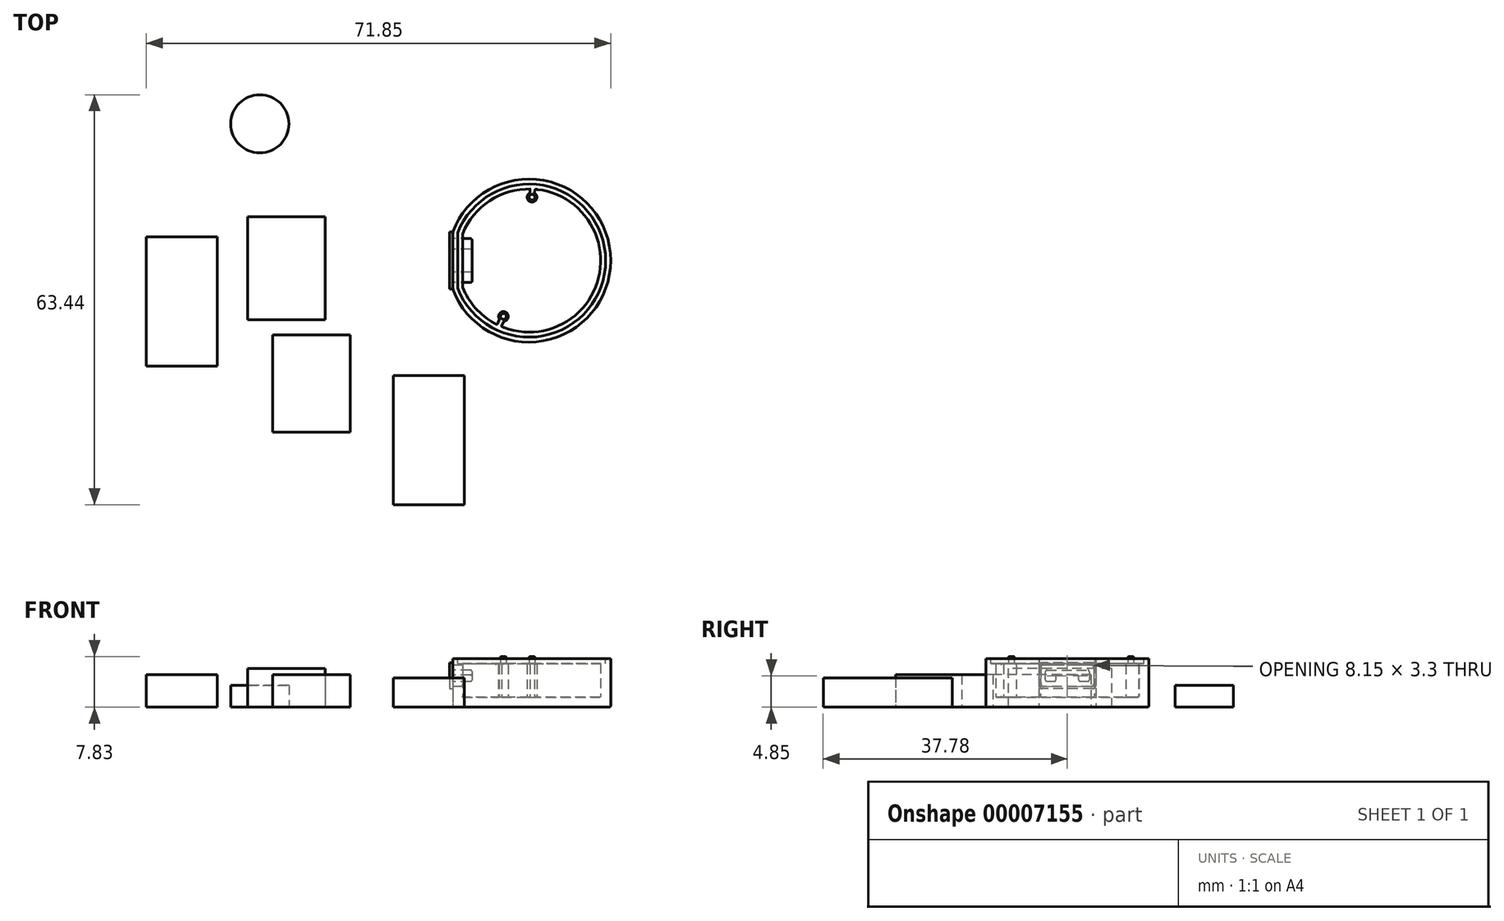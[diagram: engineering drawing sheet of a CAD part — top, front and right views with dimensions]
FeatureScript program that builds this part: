
annotation { "Feature Type Name" : "Feature", "Feature Type Description" : "" }
export const myFeature = defineFeature(function(context is Context, id is Id, definition is map)
    precondition{}
    {
        {
            var Q0;
            Q0=qCreatedBy(makeId("Top.planeOp"),FACE);
            var sketch = newSketch(context, id + "F0", { "sketchPlane" : qUnion([Q0])});
            skCircle(sketch, "E0", {"center": v(0, 0) * mm, "radius": 12.62 * mm});
            skLineSegment(sketch, "E1.bottom", {"start": v(-11.82, 4.42) * mm, "end": v(-39.46, 4.42) * mm});
            skLineSegment(sketch, "E1.top", {"start": v(-11.82, -4.42) * mm, "end": v(-39.46, -4.43) * mm});
            skLineSegment(sketch, "E1.left", {"start": v(-11.82, 4.43) * mm, "end": v(-11.82, -4.42) * mm});
            skLineSegment(sketch, "E1.right", {"start": v(-39.46, 4.42) * mm, "end": v(-39.46, -4.43) * mm});
            skSolve(sketch);
        }
        {
            var Q0;
            {var subQ0=sQuery(id+"F0.wireOp",EDGE,"E1.left");Q0=makeQuery(id+"F0.imprint","IMPRINT",FACE,{"disambiguationData":[TD([[makeQuery(id+"F0.imprint","IMPRINT",EDGE,{"derivedFrom":subQ0}),1.0]])]});}
            extrude(context, id + "F1", {"entities" : qUnion([Q0]), "depth" : 7.5 * mm});
        }
        {
            var Q0;
            Q0=makeQuery(id+"F1.opExtrude","CAP_FACE",FACE,{"disambiguationData":[OSD([sQuery(id+"F0.wireOp",EDGE,"E0"),sQuery(id+"F0.wireOp",EDGE,"E1.left")])],"isStart":false});
            shell(context, id + "F2", {"entities" : qUnion([Q0]), "thickness" : 1.55 * mm});
        }
        {
            var Q0;
            Q0=makeQuery(id+"F1.opExtrude","CAP_FACE",FACE,{"disambiguationData":[OSD([sQuery(id+"F0.wireOp",EDGE,"E0"),sQuery(id+"F0.wireOp",EDGE,"E1.left")])],"isStart":false});
            var sketch = newSketch(context, id + "F3", { "sketchPlane" : qUnion([Q0])});
            skLineSegment(sketch, "E2", {"start": v(-11.82, 4.42) * mm, "end": v(-10.27, 4.13) * mm, "construction": true});
            skLineSegment(sketch, "E3", {"start": v(-11.82, -4.42) * mm, "end": v(-10.27, -4.13) * mm, "construction": true});
            skCircle(sketch, "E4", {"center": v(0, 0) * mm, "radius": 11.85 * mm});
            skLineSegment(sketch, "E5", {"start": v(-11.05, 4.28) * mm, "end": v(-11.05, -4.28) * mm});
            skSolve(sketch);
        }
        {
            var Q0;
            {var subQ2=sQuery(id+"F3.wireOp",EDGE,"E5");Q0=makeQuery(id+"F3.imprint","IMPRINT",FACE,{"disambiguationData":[TD([[makeQuery(id+"F3.imprint","IMPRINT",EDGE,{"derivedFrom":subQ2}),1.0]])]});}
            extrude(context, id + "F4", {"entities" : qUnion([Q0]), "operationType" : NewBodyOperationType.REMOVE, "oppositeDirection" : true, "depth" : .775 * mm});
        }
        {
            var Q0;
            Q0=makeQuery(id+"F2.opShell","OFFSET_FACE",FACE,{"disambiguationData":[OSD([sQuery(id+"F0.wireOp",EDGE,"E0"),sQuery(id+"F0.wireOp",EDGE,"E1.left")])]});
            var sketch = newSketch(context, id + "F5", { "sketchPlane" : qUnion([Q0])});
            skLineSegment(sketch, "E6", {"start": v(0, 0) * mm, "end": v(0, 11.08) * mm, "construction": true});
            skCircle(sketch, "E7", {"center": v(0.46, 9.8) * mm, "radius": 0.75 * mm});
            skLineSegment(sketch, "E8", {"start": v(0, 0) * mm, "end": v(0, -11.08) * mm});
            skCircle(sketch, "E9", {"center": v(-3.97, -8.64) * mm, "radius": 0.75 * mm});
            skLineSegment(sketch, "E10", {"start": v(0, 0) * mm, "end": v(0.67, 14.46) * mm, "construction": true});
            skLineSegment(sketch, "E11", {"start": v(0.9, 11.1) * mm, "end": v(0.84, 9.9) * mm});
            skLineSegment(sketch, "E12", {"start": v(0.84, 9.9) * mm, "end": v(0.09, 9.93) * mm});
            skLineSegment(sketch, "E13", {"start": v(0.09, 9.93) * mm, "end": v(0.14, 11.14) * mm});
            skLineSegment(sketch, "E14", {"start": v(0.14, 11.14) * mm, "end": v(0.9, 11.1) * mm});
            skLineSegment(sketch, "E15", {"start": v(0, 0) * mm, "end": v(-6.04, -13.15) * mm, "construction": true});
            skLineSegment(sketch, "E16", {"start": v(-5.02, -10.04) * mm, "end": v(-4.3, -8.48) * mm});
            skLineSegment(sketch, "E17", {"start": v(-4.3, -8.48) * mm, "end": v(-3.62, -8.79) * mm});
            skLineSegment(sketch, "E18", {"start": v(-3.62, -8.79) * mm, "end": v(-4.35, -10.38) * mm});
            skLineSegment(sketch, "E19", {"start": v(-4.35, -10.38) * mm, "end": v(-5.02, -10.04) * mm});
            skSolve(sketch);
        }
        {
            var Q0;
            {var subQ4=sQuery(id+"F5.wireOp",EDGE,"E11");var subQ6=sQuery(id+"F5.wireOp",EDGE,"E7");var subQ8=makeQuery(id+"F5.imprint","INTERSECT",VERTEX,{"derivedFrom":[subQ6,subQ4]});Q0=makeQuery(id+"F5.imprint","IMPRINT",FACE,{"disambiguationData":[TD([[makeQuery(id+"F5.imprint","IMPRINT",EDGE,{"disambiguationData":[TD([[subQ8,-1.0]])],"derivedFrom":subQ6}),-1.0]])]});}
            var Q1;
            {var subQ3=sQuery(id+"F5.wireOp",EDGE,"E12");Q1=makeQuery(id+"F5.imprint","IMPRINT",FACE,{"disambiguationData":[TD([[makeQuery(id+"F5.imprint","IMPRINT",EDGE,{"derivedFrom":subQ3}),-1.0]])]});}
            var Q2;
            {var subQ3=sQuery(id+"F5.wireOp",EDGE,"E12");Q2=makeQuery(id+"F5.imprint","IMPRINT",FACE,{"disambiguationData":[TD([[makeQuery(id+"F5.imprint","IMPRINT",EDGE,{"derivedFrom":subQ3}),1.0]])]});}
            var Q3;
            {var subQ3=sQuery(id+"F5.wireOp",EDGE,"E17");Q3=makeQuery(id+"F5.imprint","IMPRINT",FACE,{"disambiguationData":[TD([[makeQuery(id+"F5.imprint","IMPRINT",EDGE,{"derivedFrom":subQ3}),1.0]])]});}
            var Q4;
            {var subQ3=sQuery(id+"F5.wireOp",EDGE,"E17");Q4=makeQuery(id+"F5.imprint","IMPRINT",FACE,{"disambiguationData":[TD([[makeQuery(id+"F5.imprint","IMPRINT",EDGE,{"derivedFrom":subQ3}),-1.0]])]});}
            var Q5;
            {var subQ4=sQuery(id+"F5.wireOp",EDGE,"E16");var subQ6=sQuery(id+"F5.wireOp",EDGE,"E9");var subQ8=makeQuery(id+"F5.imprint","INTERSECT",VERTEX,{"derivedFrom":[subQ6,subQ4]});Q5=makeQuery(id+"F5.imprint","IMPRINT",FACE,{"disambiguationData":[TD([[makeQuery(id+"F5.imprint","IMPRINT",EDGE,{"disambiguationData":[TD([[subQ8,-1.0]])],"derivedFrom":subQ6}),-1.0]])]});}
            var Q6;
            Q6=makeQuery(id+"F4.boolean.opBoolean","COPY",FACE,{"derivedFrom":makeQuery(id+"F4.opExtrude","CAP_FACE",FACE,{"disambiguationData":[OSD([sQuery(id+"F0.wireOp",EDGE,"E0"),sQuery(id+"F0.wireOp",EDGE,"E1.left"),sQuery(id+"F3.wireOp",EDGE,"E4"),sQuery(id+"F3.wireOp",EDGE,"E5")])],"isStart":false})});
            extrude(context, id + "F6", {"entities" : qUnion([Q0, Q1, Q2, Q3, Q4, Q5]), "operationType" : NewBodyOperationType.ADD, "endBound" : BoundingType.UP_TO_SURFACE, "endBoundEntityFace" : qUnion([Q6]), "depth" : 5 * mm});
        }
        {
            var Q0;
            {var subQ0=sQuery(id+"F0.wireOp",EDGE,"E0");Q0=makeQuery(id+"F6.boolean.opBoolean","MERGE",FACE,{"derivedFrom":[makeQuery(id+"F4.boolean.opBoolean","COPY",FACE,{"derivedFrom":makeQuery(id+"F4.opExtrude","CAP_FACE",FACE,{"disambiguationData":[OSD([subQ0,sQuery(id+"F0.wireOp",EDGE,"E1.left"),sQuery(id+"F3.wireOp",EDGE,"E4"),sQuery(id+"F3.wireOp",EDGE,"E5")])],"isStart":false})}),makeQuery(id+"F6.opExtrude","CAP_FACE",FACE,{"disambiguationData":[OSD([subQ0,sQuery(id+"F5.wireOp",EDGE,"E7"),sQuery(id+"F5.wireOp",EDGE,"E11"),sQuery(id+"F5.wireOp",EDGE,"E13")])],"isStart":false}),makeQuery(id+"F6.opExtrude","CAP_FACE",FACE,{"disambiguationData":[OSD([subQ0,sQuery(id+"F5.wireOp",EDGE,"E9"),sQuery(id+"F5.wireOp",EDGE,"E16"),sQuery(id+"F5.wireOp",EDGE,"E18")])],"isStart":false})]});}
            var sketch = newSketch(context, id + "F7", { "sketchPlane" : qUnion([Q0])});
            skCircle(sketch, "E20", {"center": v(0.46, 9.8) * mm, "radius": 0.45 * mm});
            skCircle(sketch, "E21", {"center": v(-3.97, -8.64) * mm, "radius": 0.45 * mm});
            skSolve(sketch);
        }
        {
            var Q0;
            Q0=makeQuery(id+"F7.imprint","IMPRINT",FACE,{"disambiguationData":[TD([[makeQuery(id+"F7.imprint","IMPRINT",EDGE,{"derivedFrom":sQuery(id+"F7.wireOp",EDGE,"E20")}),1.0]])]});
            var Q1;
            Q1=makeQuery(id+"F7.imprint","IMPRINT",FACE,{"disambiguationData":[TD([[makeQuery(id+"F7.imprint","IMPRINT",EDGE,{"derivedFrom":sQuery(id+"F7.wireOp",EDGE,"E21")}),1.0]])]});
            extrude(context, id + "F8", {"entities" : qUnion([Q0, Q1]), "operationType" : NewBodyOperationType.ADD, "depth" : 1.1 * mm});
        }
        {
            var Q0;
            Q0=makeQuery(id+"F1.opExtrude","SWEPT_FACE",FACE,{"disambiguationData":[OSD([sQuery(id+"F0.wireOp",EDGE,"E1.left")])]});
            var sketch = newSketch(context, id + "F9", { "sketchPlane" : qUnion([Q0])});
            skLineSegment(sketch, "E22.bottom", {"start": v(-3.73, 6.5) * mm, "end": v(3.73, 6.5) * mm});
            skLineSegment(sketch, "E22.top", {"start": v(-3.73, 3.2) * mm, "end": v(3.73, 3.2) * mm});
            skLineSegment(sketch, "E22.left", {"start": v(-4.08, 6.15) * mm, "end": v(-4.08, 3.55) * mm});
            skLineSegment(sketch, "E22.right", {"start": v(4.08, 6.15) * mm, "end": v(4.08, 3.55) * mm});
            skLineSegment(sketch, "E23", {"start": v(0, 0) * mm, "end": v(0, 7.5) * mm, "construction": true});
            skPoint(sketch, "E24.visualSharp", {"position": v(-4.08, 6.5) * mm});
            skArc(sketch, "E24.filletArc", {"start": v(-3.73, 6.5) * mm, "mid": v(-3.97, 6.4) * mm, "end": v(-4.08, 6.15) * mm});
            skPoint(sketch, "E25.visualSharp", {"position": v(-4.08, 3.2) * mm});
            skArc(sketch, "E25.filletArc", {"start": v(-4.08, 3.55) * mm, "mid": v(-3.97, 3.3) * mm, "end": v(-3.73, 3.2) * mm});
            skPoint(sketch, "E26.visualSharp", {"position": v(4.08, 3.2) * mm});
            skArc(sketch, "E26.filletArc", {"start": v(3.73, 3.2) * mm, "mid": v(3.97, 3.3) * mm, "end": v(4.08, 3.55) * mm});
            skPoint(sketch, "E27.visualSharp", {"position": v(4.08, 6.5) * mm});
            skArc(sketch, "E27.filletArc", {"start": v(4.08, 6.15) * mm, "mid": v(3.97, 6.4) * mm, "end": v(3.73, 6.5) * mm});
            skSolve(sketch);
        }
        {
            var Q0;
            Q0=makeQuery(id+"F9.imprint","IMPRINT",FACE,{"disambiguationData":[TD([[makeQuery(id+"F9.imprint","IMPRINT",EDGE,{"derivedFrom":sQuery(id+"F9.wireOp",EDGE,"E22.bottom")}),-1.0]])]});
            extrude(context, id + "F10", {"entities" : qUnion([Q0]), "operationType" : NewBodyOperationType.REMOVE, "endBound" : BoundingType.UP_TO_NEXT, "oppositeDirection" : true, "depth" : 25 * mm});
        }
        {
            var Q0;
            Q0=makeQuery(id+"F1.opExtrude","CAP_EDGE",EDGE,{"disambiguationData":[OSD([sQuery(id+"F0.wireOp",EDGE,"E0")])],"isStart":true});
            var Q1;
            Q1=makeQuery(id+"F1.opExtrude","CAP_EDGE",EDGE,{"disambiguationData":[OSD([sQuery(id+"F0.wireOp",EDGE,"E1.left")])],"isStart":true});
            fillet(context, id + "F11", {"entities" : qUnion([Q0, Q1]), "radius" : .25 * mm, "tangentPropagation" : true, "allowEdgeOverflow" : false});
        }
        {
            var Q0;
            Q0=makeQuery(id+"F10.boolean.opBoolean","COPY",EDGE,{"derivedFrom":makeQuery(id+"F10.opExtrude","CAP_EDGE",EDGE,{"disambiguationData":[OSD([sQuery(id+"F9.wireOp",EDGE,"E22.top")])],"isStart":true})});
            var Q1;
            Q1=makeQuery(id+"F10.boolean.opBoolean","COPY",EDGE,{"derivedFrom":makeQuery(id+"F10.opExtrude","CAP_EDGE",EDGE,{"disambiguationData":[OSD([sQuery(id+"F9.wireOp",EDGE,"E22.top")])],"isStart":false})});
            var Q2;
            Q2=makeQuery(id+"F6.opExtrude","CAP_EDGE",EDGE,{"disambiguationData":[OSD([sQuery(id+"F5.wireOp",EDGE,"E9")])],"isStart":false});
            var Q3;
            Q3=makeQuery(id+"F6.opExtrude","CAP_EDGE",EDGE,{"disambiguationData":[OSD([sQuery(id+"F5.wireOp",EDGE,"E18")])],"isStart":false});
            var Q4;
            Q4=makeQuery(id+"F8.opExtrude","CAP_EDGE",EDGE,{"disambiguationData":[OSD([sQuery(id+"F7.wireOp",EDGE,"E21")])],"isStart":false});
            var Q5;
            Q5=makeQuery(id+"F6.opExtrude","CAP_EDGE",EDGE,{"disambiguationData":[OSD([sQuery(id+"F5.wireOp",EDGE,"E16")])],"isStart":false});
            var Q6;
            Q6=makeQuery(id+"F6.opExtrude","SWEPT_EDGE",EDGE,{"disambiguationData":[OSD([sQuery(id+"F0.wireOp",EDGE,"E0"),sQuery(id+"F5.wireOp",EDGE,"E16")])]});
            var Q7;
            Q7=makeQuery(id+"F6.opExtrude","CAP_EDGE",EDGE,{"disambiguationData":[OSD([sQuery(id+"F5.wireOp",EDGE,"E9")])],"isStart":true});
            var Q8;
            Q8=makeQuery(id+"F6.opExtrude","CAP_EDGE",EDGE,{"disambiguationData":[OSD([sQuery(id+"F5.wireOp",EDGE,"E16")])],"isStart":true});
            var Q9;
            Q9=makeQuery(id+"F6.opExtrude","CAP_EDGE",EDGE,{"disambiguationData":[OSD([sQuery(id+"F5.wireOp",EDGE,"E18")])],"isStart":true});
            var Q10;
            Q10=makeQuery(id+"F6.opExtrude","SWEPT_EDGE",EDGE,{"disambiguationData":[OSD([sQuery(id+"F5.wireOp",EDGE,"E9"),sQuery(id+"F5.wireOp",EDGE,"E18")])]});
            var Q11;
            Q11=makeQuery(id+"F6.opExtrude","SWEPT_EDGE",EDGE,{"disambiguationData":[OSD([sQuery(id+"F0.wireOp",EDGE,"E0"),sQuery(id+"F5.wireOp",EDGE,"E18")])]});
            var Q12;
            Q12=makeQuery(id+"F6.opExtrude","SWEPT_EDGE",EDGE,{"disambiguationData":[OSD([sQuery(id+"F5.wireOp",EDGE,"E9"),sQuery(id+"F5.wireOp",EDGE,"E16")])]});
            var Q13;
            Q13=makeQuery(id+"F6.opExtrude","CAP_EDGE",EDGE,{"disambiguationData":[OSD([sQuery(id+"F5.wireOp",EDGE,"E13")])],"isStart":false});
            var Q14;
            Q14=makeQuery(id+"F6.opExtrude","CAP_EDGE",EDGE,{"disambiguationData":[OSD([sQuery(id+"F5.wireOp",EDGE,"E7")])],"isStart":false});
            var Q15;
            Q15=makeQuery(id+"F8.opExtrude","CAP_EDGE",EDGE,{"disambiguationData":[OSD([sQuery(id+"F7.wireOp",EDGE,"E20")])],"isStart":false});
            var Q16;
            Q16=makeQuery(id+"F6.opExtrude","CAP_EDGE",EDGE,{"disambiguationData":[OSD([sQuery(id+"F5.wireOp",EDGE,"E11")])],"isStart":false});
            var Q17;
            {var subQ0=sQuery(id+"F5.wireOp",EDGE,"E13");var subQ1=sQuery(id+"F0.wireOp",EDGE,"E0");Q17=makeQuery(id+"F6.boolean.opBoolean","SPLIT",EDGE,{"disambiguationData":[TD([makeQuery(id+"F6.opExtrude","SWEPT_FACE",FACE,{"disambiguationData":[OSD([subQ0])]})])],"derivedFrom":makeQuery(id+"F4.boolean.opBoolean","COPY",EDGE,{"derivedFrom":makeQuery(id+"F4.opExtrude","CAP_EDGE",EDGE,{"disambiguationData":[OSD([subQ1])],"isStart":false})})});}
            var Q18;
            Q18=makeQuery(id+"F6.opExtrude","SWEPT_EDGE",EDGE,{"disambiguationData":[OSD([sQuery(id+"F5.wireOp",EDGE,"E7"),sQuery(id+"F5.wireOp",EDGE,"E13")])]});
            var Q19;
            Q19=makeQuery(id+"F6.opExtrude","CAP_EDGE",EDGE,{"disambiguationData":[OSD([sQuery(id+"F5.wireOp",EDGE,"E13")])],"isStart":true});
            var Q20;
            Q20=makeQuery(id+"F6.opExtrude","CAP_EDGE",EDGE,{"disambiguationData":[OSD([sQuery(id+"F5.wireOp",EDGE,"E7")])],"isStart":true});
            var Q21;
            Q21=makeQuery(id+"F6.opExtrude","SWEPT_EDGE",EDGE,{"disambiguationData":[OSD([sQuery(id+"F5.wireOp",EDGE,"E7"),sQuery(id+"F5.wireOp",EDGE,"E11")])]});
            var Q22;
            Q22=makeQuery(id+"F6.opExtrude","SWEPT_EDGE",EDGE,{"disambiguationData":[OSD([sQuery(id+"F0.wireOp",EDGE,"E0"),sQuery(id+"F5.wireOp",EDGE,"E11")])]});
            var Q23;
            Q23=makeQuery(id+"F6.opExtrude","CAP_EDGE",EDGE,{"disambiguationData":[OSD([sQuery(id+"F5.wireOp",EDGE,"E11")])],"isStart":true});
            var Q24;
            {var subQ0=sQuery(id+"F0.wireOp",EDGE,"E0");Q24=makeQuery(id+"F6.boolean.opBoolean","SPLIT",EDGE,{"disambiguationData":[TD([makeQuery(id+"F6.opExtrude","SWEPT_FACE",FACE,{"disambiguationData":[OSD([sQuery(id+"F5.wireOp",EDGE,"E11")])]})])],"derivedFrom":makeQuery(id+"F2.opShell","OFFSET_EDGE",EDGE,{"disambiguationData":[OSD([subQ0]),TDD([makeQuery(id+"F1.opExtrude","CAP_EDGE",EDGE,{"disambiguationData":[OSD([subQ0])],"isStart":true})])]})});}
            var Q25;
            {var subQ0=sQuery(id+"F0.wireOp",EDGE,"E0");Q25=makeQuery(id+"F6.boolean.opBoolean","SPLIT",EDGE,{"disambiguationData":[TD([makeQuery(id+"F6.opExtrude","SWEPT_FACE",FACE,{"disambiguationData":[OSD([sQuery(id+"F5.wireOp",EDGE,"E13")])]})])],"derivedFrom":makeQuery(id+"F2.opShell","OFFSET_EDGE",EDGE,{"disambiguationData":[OSD([subQ0]),TDD([makeQuery(id+"F1.opExtrude","CAP_EDGE",EDGE,{"disambiguationData":[OSD([subQ0])],"isStart":true})])]})});}
            fillet(context, id + "F12", {"entities" : qUnion([Q0, Q1, Q2, Q3, Q4, Q5, Q6, Q7, Q8, Q9, Q10, Q11, Q12, Q13, Q14, Q15, Q16, Q17, Q18, Q19, Q20, Q21, Q22, Q23, Q24, Q25]), "radius" : .15 * mm, "tangentPropagation" : true, "allowEdgeOverflow" : false});
        }
        {
            var Q0;
            Q0=makeQuery(id+"F1.opExtrude","SWEPT_FACE",FACE,{"disambiguationData":[OSD([sQuery(id+"F0.wireOp",EDGE,"E1.left")])]});
            var sketch = newSketch(context, id + "F13", { "sketchPlane" : qUnion([Q0])});
            skLineSegment(sketch, "E28.rect.bottom", {"start": v(-3.93, 2.85) * mm, "end": v(3.93, 2.85) * mm});
            skLineSegment(sketch, "E28.rect.top", {"start": v(-3.93, 6.85) * mm, "end": v(3.93, 6.85) * mm});
            skLineSegment(sketch, "E28.rect.left", {"start": v(-4.43, 3.35) * mm, "end": v(-4.43, 6.35) * mm});
            skLineSegment(sketch, "E28.rect.right", {"start": v(4.43, 3.35) * mm, "end": v(4.43, 6.35) * mm});
            skPoint(sketch, "E28.rect.middle", {"position": v(0, 4.85) * mm});
            skPoint(sketch, "E29.visualSharp", {"position": v(-4.43, 6.85) * mm});
            skArc(sketch, "E29.filletArc", {"start": v(-3.93, 6.85) * mm, "mid": v(-4.28, 6.7) * mm, "end": v(-4.43, 6.35) * mm});
            skPoint(sketch, "E30.visualSharp", {"position": v(-4.43, 2.85) * mm});
            skArc(sketch, "E30.filletArc", {"start": v(-4.43, 3.35) * mm, "mid": v(-4.28, 3) * mm, "end": v(-3.93, 2.85) * mm});
            skPoint(sketch, "E31.visualSharp", {"position": v(4.43, 2.85) * mm});
            skArc(sketch, "E31.filletArc", {"start": v(3.93, 2.85) * mm, "mid": v(4.28, 3) * mm, "end": v(4.43, 3.35) * mm});
            skPoint(sketch, "E32.visualSharp", {"position": v(4.43, 6.85) * mm});
            skArc(sketch, "E32.filletArc", {"start": v(4.43, 6.35) * mm, "mid": v(4.28, 6.7) * mm, "end": v(3.93, 6.85) * mm});
            skSolve(sketch);
        }
        {
            var Q0;
            Q0 = qSketchRegion(id + "F13", true);
            extrude(context, id + "F14", {"entities" : qUnion([Q0]), "depth" : .5 * mm});
        }
        {
            var Q0;
            Q0=makeQuery(id+"F14.opExtrude","CAP_FACE",FACE,{"disambiguationData":[OSD([sQuery(id+"F13.wireOp",EDGE,"E28.rect.bottom"),sQuery(id+"F13.wireOp",EDGE,"E28.rect.top"),sQuery(id+"F13.wireOp",EDGE,"E28.rect.left"),sQuery(id+"F13.wireOp",EDGE,"E28.rect.right"),sQuery(id+"F13.wireOp",EDGE,"E29.filletArc"),sQuery(id+"F13.wireOp",EDGE,"E30.filletArc"),sQuery(id+"F13.wireOp",EDGE,"E31.filletArc"),sQuery(id+"F13.wireOp",EDGE,"E32.filletArc")])],"isStart":true});
            var sketch = newSketch(context, id + "F15", { "sketchPlane" : qUnion([Q0])});
            skLineSegment(sketch, "E33", {"start": v(0, 6.85) * mm, "end": v(0, 2.85) * mm, "construction": true});
            skLineSegment(sketch, "E34", {"start": v(-4.43, 4.85) * mm, "end": v(4.43, 4.85) * mm, "construction": true});
            skLineSegment(sketch, "E35", {"start": v(-3.15, 5.72) * mm, "end": v(3.15, 5.72) * mm});
            skLineSegment(sketch, "E36", {"start": v(3.4, 5.47) * mm, "end": v(3.4, 4.22) * mm});
            skLineSegment(sketch, "E37", {"start": v(3.15, 3.97) * mm, "end": v(2.02, 3.97) * mm});
            skLineSegment(sketch, "E38", {"start": v(1.77, 4.22) * mm, "end": v(1.77, 4.7) * mm});
            skLineSegment(sketch, "E39", {"start": v(1.53, 4.95) * mm, "end": v(-1.53, 4.95) * mm});
            skLineSegment(sketch, "E40", {"start": v(-1.77, 4.7) * mm, "end": v(-1.77, 4.22) * mm});
            skLineSegment(sketch, "E41", {"start": v(-2.02, 3.97) * mm, "end": v(-3.15, 3.97) * mm});
            skLineSegment(sketch, "E42", {"start": v(-3.4, 4.22) * mm, "end": v(-3.4, 5.47) * mm});
            skPoint(sketch, "E43.visualSharp", {"position": v(-3.4, 5.72) * mm});
            skArc(sketch, "E43.filletArc", {"start": v(-3.15, 5.72) * mm, "mid": v(-3.33, 5.65) * mm, "end": v(-3.4, 5.47) * mm});
            skPoint(sketch, "E44.visualSharp", {"position": v(-3.4, 3.97) * mm});
            skArc(sketch, "E44.filletArc", {"start": v(-3.4, 4.22) * mm, "mid": v(-3.33, 4.05) * mm, "end": v(-3.15, 3.97) * mm});
            skPoint(sketch, "E45.visualSharp", {"position": v(-1.77, 3.97) * mm});
            skArc(sketch, "E45.filletArc", {"start": v(-2.02, 3.97) * mm, "mid": v(-1.85, 4.05) * mm, "end": v(-1.77, 4.22) * mm});
            skPoint(sketch, "E46.visualSharp", {"position": v(-1.78, 4.95) * mm});
            skArc(sketch, "E46.filletArc", {"start": v(-1.53, 4.95) * mm, "mid": v(-1.7, 4.88) * mm, "end": v(-1.77, 4.7) * mm});
            skPoint(sketch, "E47.visualSharp", {"position": v(1.77, 4.95) * mm});
            skArc(sketch, "E47.filletArc", {"start": v(1.77, 4.7) * mm, "mid": v(1.7, 4.88) * mm, "end": v(1.53, 4.95) * mm});
            skPoint(sketch, "E48.visualSharp", {"position": v(1.78, 3.97) * mm});
            skArc(sketch, "E48.filletArc", {"start": v(1.78, 4.22) * mm, "mid": v(1.85, 4.05) * mm, "end": v(2.02, 3.97) * mm});
            skPoint(sketch, "E49.visualSharp", {"position": v(3.4, 3.97) * mm});
            skArc(sketch, "E49.filletArc", {"start": v(3.15, 3.97) * mm, "mid": v(3.33, 4.05) * mm, "end": v(3.4, 4.22) * mm});
            skPoint(sketch, "E50.visualSharp", {"position": v(3.4, 5.72) * mm});
            skArc(sketch, "E50.filletArc", {"start": v(3.4, 5.47) * mm, "mid": v(3.33, 5.65) * mm, "end": v(3.15, 5.72) * mm});
            skSolve(sketch);
        }
        {
            var Q0;
            Q0 = qSketchRegion(id + "F15", true);
            extrude(context, id + "F16", {"entities" : qUnion([Q0]), "operationType" : NewBodyOperationType.ADD, "depth" : 3 * mm});
        }
        {
            var Q0;
            Q0=makeQuery(id+"F16.opExtrude","CAP_EDGE",EDGE,{"disambiguationData":[OSD([sQuery(id+"F15.wireOp",EDGE,"E41")])],"isStart":false});
            fillet(context, id + "F17", {"entities" : qUnion([Q0]), "radius" : .25 * mm, "tangentPropagation" : true, "allowEdgeOverflow" : false});
        }
        {
            var Q0;
            Q0=qCreatedBy(makeId("Top.planeOp"),FACE);
            var sketch = newSketch(context, id + "F18", { "sketchPlane" : qUnion([Q0])});
            skLineSegment(sketch, "E51.bottom", {"start": v(-59.22, 3.68) * mm, "end": v(-48.22, 3.68) * mm});
            skLineSegment(sketch, "E51.top", {"start": v(-59.22, -16.32) * mm, "end": v(-48.22, -16.32) * mm});
            skLineSegment(sketch, "E51.left", {"start": v(-59.22, 3.68) * mm, "end": v(-59.22, -16.32) * mm});
            skLineSegment(sketch, "E51.right", {"start": v(-48.22, 3.68) * mm, "end": v(-48.22, -16.32) * mm});
            skSolve(sketch);
        }
        {
            var Q0;
            Q0=makeQuery(id+"F18.imprint","IMPRINT",FACE,{"disambiguationData":[TD([[makeQuery(id+"F18.imprint","IMPRINT",EDGE,{"derivedFrom":sQuery(id+"F18.wireOp",EDGE,"E51.bottom")}),-1.0]])]});
            extrude(context, id + "F19", {"entities" : qUnion([Q0]), "depth" : 5 * mm});
        }
        {
            var Q0;
            Q0=qCreatedBy(makeId("Top.planeOp"),FACE);
            var sketch = newSketch(context, id + "F20", { "sketchPlane" : qUnion([Q0])});
            skLineSegment(sketch, "E52.bottom", {"start": v(-43.53, 6.81) * mm, "end": v(-31.53, 6.81) * mm});
            skLineSegment(sketch, "E52.top", {"start": v(-43.53, -9.19) * mm, "end": v(-31.53, -9.19) * mm});
            skLineSegment(sketch, "E52.left", {"start": v(-43.53, 6.81) * mm, "end": v(-43.53, -9.19) * mm});
            skLineSegment(sketch, "E52.right", {"start": v(-31.53, 6.81) * mm, "end": v(-31.53, -9.19) * mm});
            skSolve(sketch);
        }
        {
            var Q0;
            Q0=makeQuery(id+"F20.imprint","IMPRINT",FACE,{"disambiguationData":[TD([[makeQuery(id+"F20.imprint","IMPRINT",EDGE,{"derivedFrom":sQuery(id+"F20.wireOp",EDGE,"E52.bottom")}),-1.0]])]});
            extrude(context, id + "F21", {"entities" : qUnion([Q0]), "depth" : 6 * mm});
        }
        {
            var Q0;
            Q0=qCreatedBy(makeId("Top.planeOp"),FACE);
            var sketch = newSketch(context, id + "F22", { "sketchPlane" : qUnion([Q0])});
            skLineSegment(sketch, "E53.bottom", {"start": v(-39.66, -11.54) * mm, "end": v(-27.66, -11.54) * mm});
            skLineSegment(sketch, "E53.top", {"start": v(-39.66, -26.54) * mm, "end": v(-27.66, -26.54) * mm});
            skLineSegment(sketch, "E53.left", {"start": v(-39.66, -11.54) * mm, "end": v(-39.66, -26.54) * mm});
            skLineSegment(sketch, "E53.right", {"start": v(-27.66, -11.54) * mm, "end": v(-27.66, -26.54) * mm});
            skSolve(sketch);
        }
        {
            var Q0;
            Q0=makeQuery(id+"F22.imprint","IMPRINT",FACE,{"disambiguationData":[TD([[makeQuery(id+"F22.imprint","IMPRINT",EDGE,{"derivedFrom":sQuery(id+"F22.wireOp",EDGE,"E53.bottom")}),-1.0]])]});
            extrude(context, id + "F23", {"entities" : qUnion([Q0]), "depth" : 5 * mm});
        }
        {
            var Q0;
            Q0=qCreatedBy(makeId("Top.planeOp"),FACE);
            var sketch = newSketch(context, id + "F24", { "sketchPlane" : qUnion([Q0])});
            skLineSegment(sketch, "E54.bottom", {"start": v(-21.02, -17.78) * mm, "end": v(-10.02, -17.78) * mm});
            skLineSegment(sketch, "E54.top", {"start": v(-21.02, -37.78) * mm, "end": v(-10.02, -37.78) * mm});
            skLineSegment(sketch, "E54.left", {"start": v(-21.02, -17.78) * mm, "end": v(-21.02, -37.78) * mm});
            skLineSegment(sketch, "E54.right", {"start": v(-10.02, -17.78) * mm, "end": v(-10.02, -37.78) * mm});
            skSolve(sketch);
        }
        {
            var Q0;
            Q0=makeQuery(id+"F24.imprint","IMPRINT",FACE,{"disambiguationData":[TD([[makeQuery(id+"F24.imprint","IMPRINT",EDGE,{"derivedFrom":sQuery(id+"F24.wireOp",EDGE,"E54.bottom")}),-1.0]])]});
            extrude(context, id + "F25", {"entities" : qUnion([Q0]), "depth" : 4.5 * mm});
        }
        {
            var Q0;
            Q0=qCreatedBy(makeId("Top.planeOp"),FACE);
            var sketch = newSketch(context, id + "F26", { "sketchPlane" : qUnion([Q0])});
            skCircle(sketch, "E55", {"center": v(-41.66, 21.16) * mm, "radius": 4.5 * mm});
            skSolve(sketch);
        }
        {
            var Q0;
            Q0=makeQuery(id+"F26.imprint","IMPRINT",FACE,{"disambiguationData":[TD([[makeQuery(id+"F26.imprint","IMPRINT",EDGE,{"derivedFrom":sQuery(id+"F26.wireOp",EDGE,"E55")}),1.0]])]});
            extrude(context, id + "F27", {"entities" : qUnion([Q0]), "depth" : 3.4 * mm});
        }
    });
